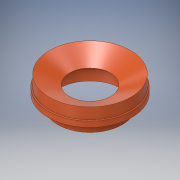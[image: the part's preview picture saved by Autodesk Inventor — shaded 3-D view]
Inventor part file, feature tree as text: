
AUTODESK INVENTOR PART (.ipt)
format: ipt  version: 2017 SP1 (Build 210196100, 196)  size: 175,104 bytes
history: native  units: in
note: dims shown in document units (in); Inventor stores cm internally (conversion verified against a paired STEP export)
features: revolve x1, sketch x1
ambient origin geometry x8: Origin, YZ Plane, XZ Plane, XY Plane, X Axis, Y Axis, Z Axis, Center Point
bodies: Solid1 (feature_tree)
feature tree (2):
  revolve  "Revolution1"  [1 undecoded]
  sketch  "Sketch1"  dims[d0=1.13in d1=3.75in d2=0.125in d3=0.1718in d5=1.0in d6=1.0in d7=90.0deg d8=0.5in d9=15.0deg d12=1.25in d13=0.25in d16=0.5in d17=0.5in d18=0.5in d19=2.5in d20=0.5in d22=0.375in d23=0.25in d25=0.234in d27=0.125in d28=0.25in d29=1.0in d30=4.25in d31=0.25in d33=0.8014in d34=15.0deg d35=0.125in d36=1.0in d37=90.0deg]
note: 1 required parameter value undecoded (feature->parameter linkage not recoverable at this tier; creation-order binding heuristic only, values carry confidence <= 0.55)
